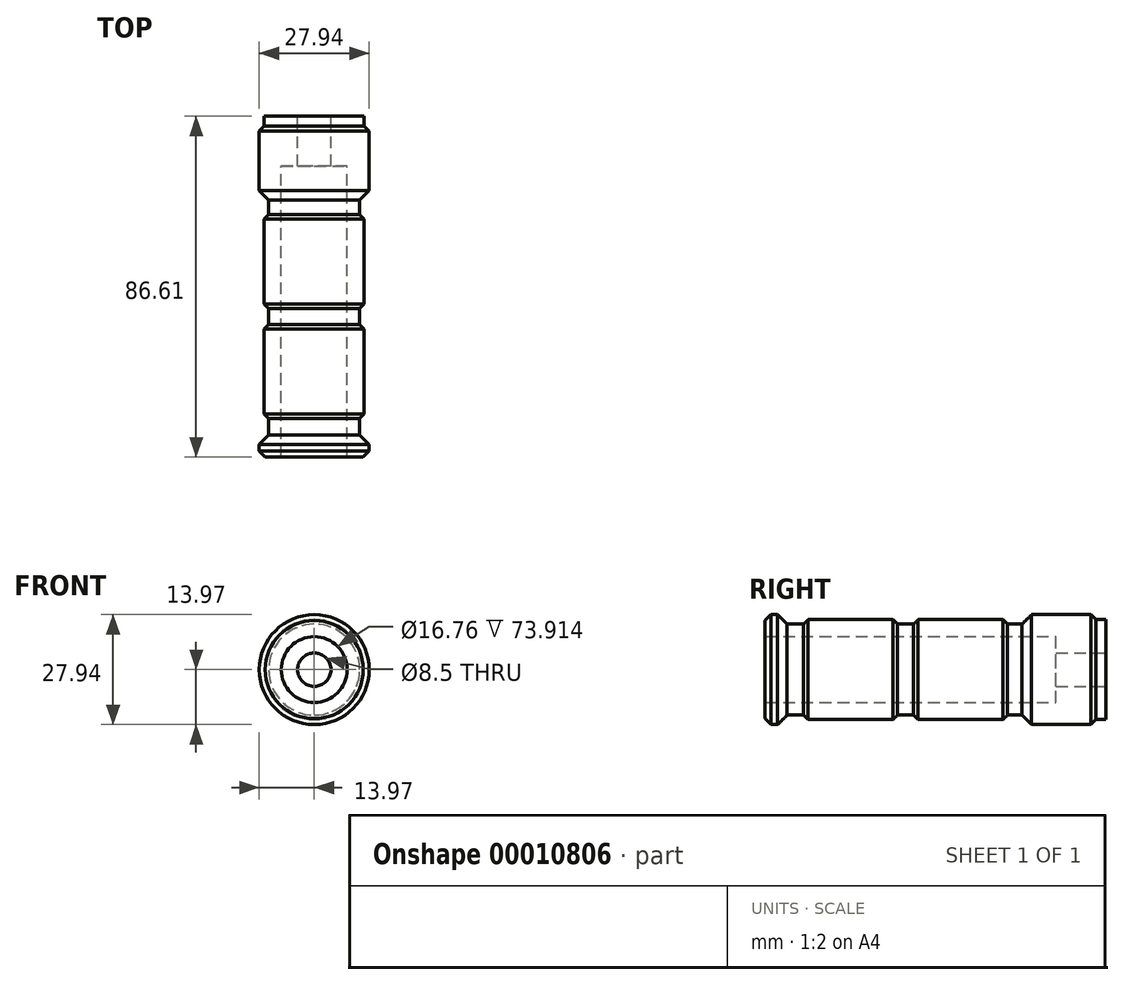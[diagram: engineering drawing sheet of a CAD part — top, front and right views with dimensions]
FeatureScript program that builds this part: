
annotation { "Feature Type Name" : "Feature", "Feature Type Description" : "" }
export const myFeature = defineFeature(function(context is Context, id is Id, definition is map)
    precondition{}
    {
        {
            var Q0;
            Q0=qCreatedBy(makeId("Front.planeOp"),FACE);
            var sketch = newSketch(context, id + "F0", { "sketchPlane" : qUnion([Q0])});
            skCircle(sketch, "E0", {"center": v(0, 0) * mm, "radius": 13.97 * mm});
            skSolve(sketch);
        }
        {
            var Q0;
            Q0=makeQuery(id+"F0.imprint","IMPRINT",FACE,{"disambiguationData":[TD([[makeQuery(id+"F0.imprint","IMPRINT",EDGE,{"derivedFrom":sQuery(id+"F0.wireOp",EDGE,"E0")}),1.0]])]});
            extrude(context, id + "F1", {"entities" : qUnion([Q0]), "depth" : 86.61 * mm});
        }
        {
            var Q0;
            Q0=qCreatedBy(makeId("Right.planeOp"),FACE);
            var sketch = newSketch(context, id + "F2", { "sketchPlane" : qUnion([Q0])});
            skLineSegment(sketch, "E1", {"start": v(0, 15.88) * mm, "end": v(-5.72, 15.87) * mm});
            skLineSegment(sketch, "E2", {"start": v(-5.71, 15.87) * mm, "end": v(-2.54, 12.7) * mm});
            skLineSegment(sketch, "E3", {"start": v(-2.54, 12.7) * mm, "end": v(0, 12.7) * mm});
            skLineSegment(sketch, "E4", {"start": v(0, 12.7) * mm, "end": v(0, 15.88) * mm});
            skSolve(sketch);
        }
        {
            var Q0;
            Q0=makeQuery(id+"F2.imprint","IMPRINT",FACE,{"disambiguationData":[TD([[makeQuery(id+"F2.imprint","IMPRINT",EDGE,{"derivedFrom":sQuery(id+"F2.wireOp",EDGE,"E1")}),1.0]])]});
            var Q1;
            Q1=makeQuery(id+"F1.opExtrude","SWEPT_FACE",FACE,{"disambiguationData":[OSD([sQuery(id+"F0.wireOp",EDGE,"E0")])]});
            revolve(context, id + "F3", {"operationType" : NewBodyOperationType.REMOVE, "entities" : qUnion([Q0]), "axis" : qUnion([Q1]), "revolveType" : RevolveType.FULL, "oppositeDirection" : true});
        }
        {
            var Q0;
            Q0=qCreatedBy(makeId("Right.planeOp"),FACE);
            var sketch = newSketch(context, id + "F4", { "sketchPlane" : qUnion([Q0])});
            skLineSegment(sketch, "E5", {"start": v(-14.99, 17.9) * mm, "end": v(-21.34, 11.56) * mm});
            skLineSegment(sketch, "E6", {"start": v(-21.34, 11.56) * mm, "end": v(-81.03, 11.56) * mm});
            skLineSegment(sketch, "E7", {"start": v(-81.03, 11.56) * mm, "end": v(-87.38, 17.9) * mm});
            skLineSegment(sketch, "E8", {"start": v(-87.38, 17.9) * mm, "end": v(-14.99, 17.9) * mm});
            skSolve(sketch);
        }
        {
            var Q0;
            Q0=makeQuery(id+"F4.imprint","IMPRINT",FACE,{"disambiguationData":[TD([[makeQuery(id+"F4.imprint","IMPRINT",EDGE,{"derivedFrom":sQuery(id+"F4.wireOp",EDGE,"E5")}),-1.0]])]});
            var Q1;
            Q1=makeQuery(id+"F1.opExtrude","SWEPT_FACE",FACE,{"disambiguationData":[OSD([sQuery(id+"F0.wireOp",EDGE,"E0")])]});
            revolve(context, id + "F5", {"operationType" : NewBodyOperationType.REMOVE, "entities" : qUnion([Q0]), "axis" : qUnion([Q1]), "revolveType" : RevolveType.FULL, "oppositeDirection" : true});
        }
        {
            var Q0;
            Q0=makeQuery(id+"F1.opExtrude","CAP_EDGE",EDGE,{"disambiguationData":[OSD([sQuery(id+"F0.wireOp",EDGE,"E0")])],"isStart":false});
            chamfer(context, id + "F6", {"entities" : qUnion([Q0]), "width" : 1.52 * mm, "tangentPropagation" : true});
        }
        {
            var Q0;
            Q0=qCreatedBy(makeId("Right.planeOp"),FACE);
            var sketch = newSketch(context, id + "F7", { "sketchPlane" : qUnion([Q0])});
            skLineSegment(sketch, "E9", {"start": v(-22.99, 9.53) * mm, "end": v(-26.16, 12.7) * mm});
            skLineSegment(sketch, "E10", {"start": v(-26.16, 12.7) * mm, "end": v(-47.75, 12.7) * mm});
            skLineSegment(sketch, "E11", {"start": v(-47.75, 12.7) * mm, "end": v(-50.93, 9.52) * mm});
            skLineSegment(sketch, "E12", {"start": v(-50.93, 9.52) * mm, "end": v(-22.99, 9.53) * mm});
            skSolve(sketch);
        }
        {
            var Q0;
            Q0=makeQuery(id+"F7.imprint","IMPRINT",FACE,{"disambiguationData":[TD([[makeQuery(id+"F7.imprint","IMPRINT",EDGE,{"derivedFrom":sQuery(id+"F7.wireOp",EDGE,"E9")}),1.0]])]});
            var Q1;
            Q1=makeQuery(id+"F5.boolean.opBoolean","COPY",FACE,{"derivedFrom":makeQuery(id+"F5.opRevolve","SWEPT_FACE",FACE,{"disambiguationData":[OSD([sQuery(id+"F4.wireOp",EDGE,"E6")])]})});
            revolve(context, id + "F8", {"operationType" : NewBodyOperationType.ADD, "entities" : qUnion([Q0]), "axis" : qUnion([Q1]), "revolveType" : RevolveType.FULL});
        }
        {
            var Q0;
            Q0=qCreatedBy(makeId("Right.planeOp"),FACE);
            var sketch = newSketch(context, id + "F9", { "sketchPlane" : qUnion([Q0])});
            skLineSegment(sketch, "E13", {"start": v(-54.1, 12.7) * mm, "end": v(-50.93, 9.53) * mm});
            skLineSegment(sketch, "E14", {"start": v(-50.93, 9.53) * mm, "end": v(-78.87, 9.52) * mm});
            skLineSegment(sketch, "E15", {"start": v(-78.87, 9.52) * mm, "end": v(-75.7, 12.7) * mm});
            skLineSegment(sketch, "E16", {"start": v(-75.7, 12.7) * mm, "end": v(-54.1, 12.7) * mm});
            skSolve(sketch);
        }
        {
            var Q0;
            Q0=makeQuery(id+"F9.imprint","IMPRINT",FACE,{"disambiguationData":[TD([[makeQuery(id+"F9.imprint","IMPRINT",EDGE,{"derivedFrom":sQuery(id+"F9.wireOp",EDGE,"E13")}),-1.0]])]});
            var Q1;
            Q1=makeQuery(id+"F8.boolean.opBoolean","SPLIT",FACE,{"disambiguationData":[TD([makeQuery(id+"F5.boolean.opBoolean","COPY",FACE,{"derivedFrom":makeQuery(id+"F5.opRevolve","SWEPT_FACE",FACE,{"disambiguationData":[OSD([sQuery(id+"F4.wireOp",EDGE,"E7")])]})})])],"derivedFrom":makeQuery(id+"F5.boolean.opBoolean","COPY",FACE,{"derivedFrom":makeQuery(id+"F5.opRevolve","SWEPT_FACE",FACE,{"disambiguationData":[OSD([sQuery(id+"F4.wireOp",EDGE,"E6")])]})})});
            revolve(context, id + "F10", {"operationType" : NewBodyOperationType.ADD, "entities" : qUnion([Q0]), "axis" : qUnion([Q1]), "revolveType" : RevolveType.FULL});
        }
        {
            var Q0;
            Q0=qCreatedBy(makeId("Front.planeOp"),FACE);
            cPlane(context, id + "F11", {"entities" : qUnion([Q0]), "cplaneType" : CPlaneType.OFFSET, "offset" : 12.7 * mm, "width" : 152.4 * mm, "height" : 152.4 * mm});
        }
        {
            var Q0;
            Q0=qCreatedBy(id+"F11.planeOp",FACE);
            var sketch = newSketch(context, id + "F12", { "sketchPlane" : qUnion([Q0])});
            skCircle(sketch, "E17", {"center": v(0, 0) * mm, "radius": 8.38 * mm});
            skSolve(sketch);
        }
        {
            var Q0;
            Q0 = qSketchRegion(id + "F12", true);
            extrude(context, id + "F13", {"entities" : qUnion([Q0]), "operationType" : NewBodyOperationType.REMOVE, "endBound" : BoundingType.THROUGH_ALL, "depth" : 25.4 * mm});
        }
        {
            var Q0;
            Q0=qCreatedBy(makeId("Front.planeOp"),FACE);
            var sketch = newSketch(context, id + "F14", { "sketchPlane" : qUnion([Q0])});
            skCircle(sketch, "E18", {"center": v(0, 0) * mm, "radius": 4.25 * mm});
            skSolve(sketch);
        }
        {
            var Q0;
            Q0=makeQuery(id+"F14.imprint","IMPRINT",FACE,{"disambiguationData":[TD([[makeQuery(id+"F14.imprint","IMPRINT",EDGE,{"derivedFrom":sQuery(id+"F14.wireOp",EDGE,"E18")}),1.0]])]});
            extrude(context, id + "F15", {"entities" : qUnion([Q0]), "operationType" : NewBodyOperationType.REMOVE, "endBound" : BoundingType.THROUGH_ALL, "depth" : 25.4 * mm});
        }
    });
